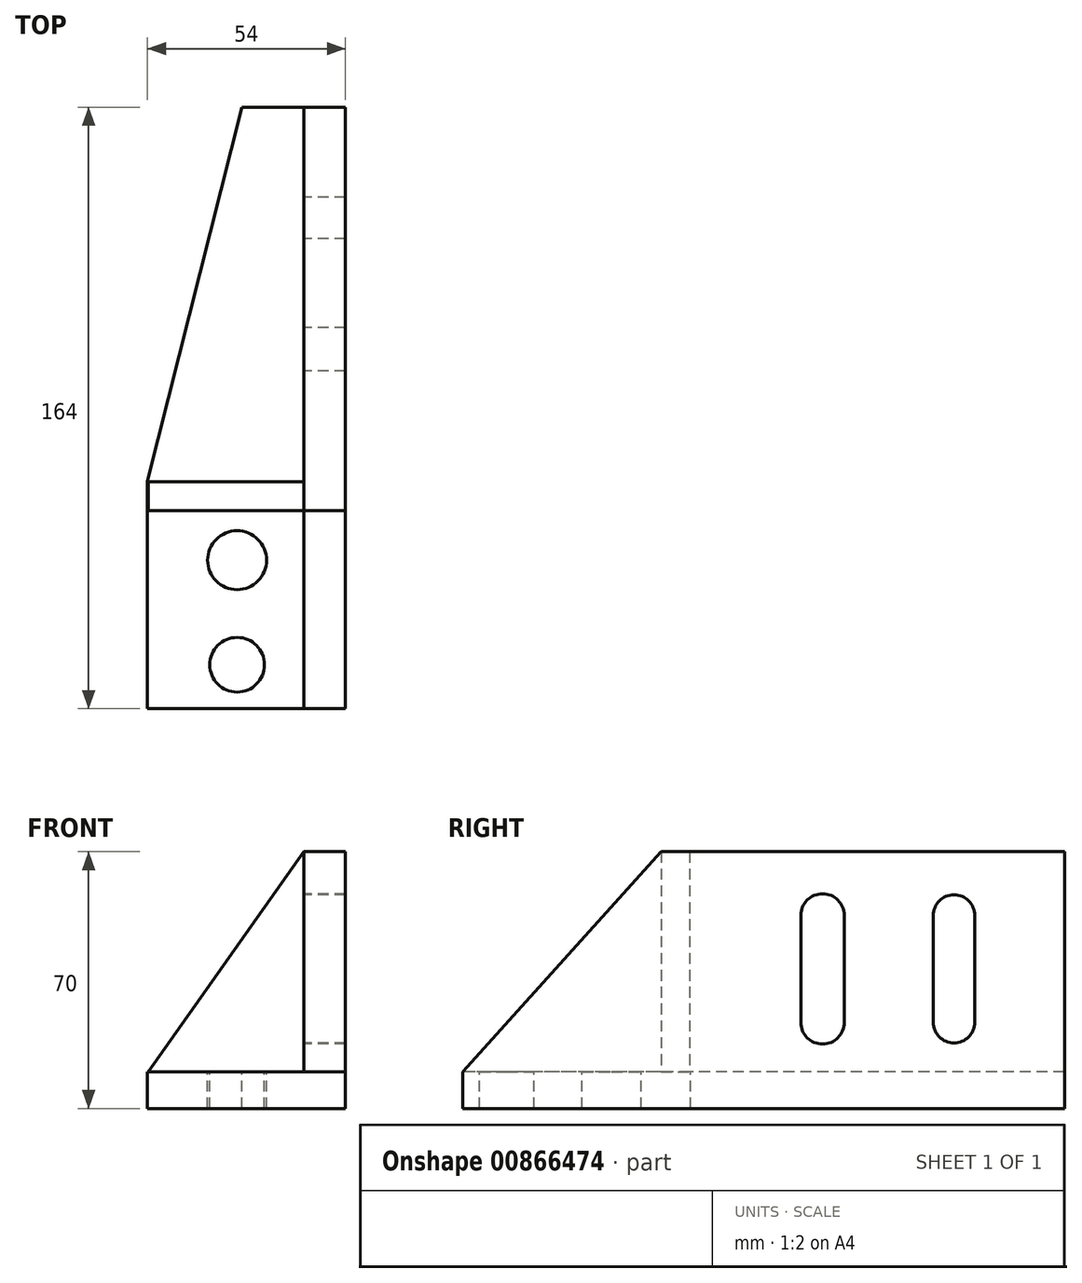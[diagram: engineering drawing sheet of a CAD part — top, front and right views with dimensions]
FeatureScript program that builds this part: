
annotation { "Feature Type Name" : "Feature", "Feature Type Description" : "" }
export const myFeature = defineFeature(function(context is Context, id is Id, definition is map)
    precondition{}
    {
        {
            var Q0;
            Q0=qCreatedBy(makeId("Top.planeOp"),FACE);
            var sketch = newSketch(context, id + "F0", { "sketchPlane" : qUnion([Q0])});
            skLineSegment(sketch, "E0.bottom", {"start": v(0, 0) * mm, "end": v(-54, 0) * mm});
            skLineSegment(sketch, "E0.top", {"start": v(0, -54) * mm, "end": v(-54, -54) * mm});
            skLineSegment(sketch, "E0.left", {"start": v(0, 0) * mm, "end": v(0, -54) * mm});
            skLineSegment(sketch, "E0.right", {"start": v(-54, 0) * mm, "end": v(-54, -54) * mm});
            skSolve(sketch);
        }
        {
            var Q0;
            Q0 = qSketchRegion(id + "F0", true);
            extrude(context, id + "F1", {"entities" : qUnion([Q0]), "depth" : 10 * mm, "offsetDistance" : 25 * mm});
        }
        {
            var Q0;
            Q0=makeQuery(id+"F1.opExtrude","SWEPT_FACE",FACE,{"disambiguationData":[OSD([sQuery(id+"F0.wireOp",EDGE,"E0.bottom")])]});
            extrude(context, id + "F2", {"entities" : qUnion([Q0]), "operationType" : NewBodyOperationType.ADD, "depth" : 110 * mm, "offsetDistance" : 25 * mm});
        }
        {
            var Q0;
            {var subQ0=sQuery(id+"F0.wireOp",EDGE,"E0.bottom");Q0=makeQuery(id+"F2.boolean.opBoolean","MERGE",FACE,{"derivedFrom":[makeQuery(id+"F1.opExtrude","CAP_FACE",FACE,{"disambiguationData":[OSD([subQ0,sQuery(id+"F0.wireOp",EDGE,"E0.top"),sQuery(id+"F0.wireOp",EDGE,"E0.left"),sQuery(id+"F0.wireOp",EDGE,"E0.right")])],"isStart":false}),makeQuery(id+"F2.opExtrude","SWEPT_FACE",FACE,{"disambiguationData":[OSD([subQ0]),TDD([makeQuery(id+"F1.opExtrude","CAP_EDGE",EDGE,{"disambiguationData":[OSD([subQ0])],"isStart":false})])]})]});}
            var sketch = newSketch(context, id + "F3", { "sketchPlane" : qUnion([Q0])});
            skLineSegment(sketch, "E1", {"start": v(-11.3, 110) * mm, "end": v(-11.3, -54) * mm});
            skSolve(sketch);
        }
        {
            var Q0;
            {var subQ0=sQuery(id+"F3.wireOp",EDGE,"E1");Q0=makeQuery(id+"F3.imprint","IMPRINT",FACE,{"disambiguationData":[TD([[makeQuery(id+"F3.imprint","IMPRINT",EDGE,{"derivedFrom":subQ0}),1.0]])]});}
            extrude(context, id + "F4", {"entities" : qUnion([Q0]), "operationType" : NewBodyOperationType.ADD, "depth" : 60 * mm, "offsetDistance" : 25 * mm});
        }
        {
            var Q0;
            Q0=makeQuery(id+"F4.opExtrude","SWEPT_FACE",FACE,{"disambiguationData":[OSD([sQuery(id+"F3.wireOp",EDGE,"E1")])]});
            var sketch = newSketch(context, id + "F5", { "sketchPlane" : qUnion([Q0])});
            skLineSegment(sketch, "E2", {"start": v(0, 70) * mm, "end": v(54, 10) * mm});
            skSolve(sketch);
        }
        {
            var Q0;
            Q0 = qSketchRegion(id + "F5", true);
            var Q1;
            {var subQ0=sQuery(id+"F5.wireOp",EDGE,"E2");Q1=makeQuery(id+"F5.imprint","IMPRINT",FACE,{"disambiguationData":[TD([[makeQuery(id+"F5.imprint","IMPRINT",EDGE,{"derivedFrom":subQ0}),1.0]])]});}
            extrude(context, id + "F6", {"entities" : qUnion([Q0, Q1]), "operationType" : NewBodyOperationType.REMOVE, "oppositeDirection" : true, "depth" : 25 * mm, "offsetDistance" : 25 * mm});
        }
        {
            var Q0;
            {var subQ0=sQuery(id+"F0.wireOp",EDGE,"E0.bottom");Q0=makeQuery(id+"F2.boolean.opBoolean","MERGE",FACE,{"derivedFrom":[makeQuery(id+"F1.opExtrude","CAP_FACE",FACE,{"disambiguationData":[OSD([subQ0,sQuery(id+"F0.wireOp",EDGE,"E0.top"),sQuery(id+"F0.wireOp",EDGE,"E0.left"),sQuery(id+"F0.wireOp",EDGE,"E0.right")])],"isStart":false}),makeQuery(id+"F2.opExtrude","SWEPT_FACE",FACE,{"disambiguationData":[OSD([subQ0]),TDD([makeQuery(id+"F1.opExtrude","CAP_EDGE",EDGE,{"disambiguationData":[OSD([subQ0])],"isStart":false})])]})]});}
            var sketch = newSketch(context, id + "F7", { "sketchPlane" : qUnion([Q0])});
            skSolve(sketch);
        }
        {
            var Q0;
            Q0=makeQuery(id+"F7.imprint","IMPRINT",FACE,{"disambiguationData":[TD([[makeQuery(id+"F7.imprint","IMPRINT",EDGE,{"derivedFrom":makeQuery(id+"F1.opExtrude","CAP_EDGE",EDGE,{"disambiguationData":[OSD([sQuery(id+"F0.wireOp",EDGE,"E0.top")])],"isStart":false})}),-1.0]])]});
            var sketch = newSketch(context, id + "F8", { "sketchPlane" : qUnion([Q0])});
            skLineSegment(sketch, "E3.bottom", {"start": v(-9.8, 0) * mm, "end": v(-53.8, 0) * mm});
            skLineSegment(sketch, "E3.top", {"start": v(-9.8, 7.85) * mm, "end": v(-53.8, 7.85) * mm});
            skLineSegment(sketch, "E3.left", {"start": v(-9.8, 0) * mm, "end": v(-9.8, 7.85) * mm});
            skLineSegment(sketch, "E3.right", {"start": v(-53.8, 0) * mm, "end": v(-53.8, 7.85) * mm});
            skSolve(sketch);
        }
        {
            var Q0;
            Q0 = qSketchRegion(id + "F8", true);
            extrude(context, id + "F9", {"entities" : qUnion([Q0]), "operationType" : NewBodyOperationType.ADD, "depth" : 60 * mm, "offsetDistance" : 25 * mm});
        }
        {
            var Q0;
            Q0=makeQuery(id+"F9.opExtrude","SWEPT_FACE",FACE,{"disambiguationData":[OSD([sQuery(id+"F8.wireOp",EDGE,"E3.bottom")])]});
            var sketch = newSketch(context, id + "F10", { "sketchPlane" : qUnion([Q0])});
            skLineSegment(sketch, "E4", {"start": v(-11.3, 70) * mm, "end": v(-53.8, 10) * mm});
            skSolve(sketch);
        }
        {
            var Q0;
            Q0 = qSketchRegion(id + "F10", true);
            var Q1;
            Q1=makeQuery(id+"F10.imprint","IMPRINT",FACE,{"disambiguationData":[TD([[makeQuery(id+"F10.imprint","IMPRINT",EDGE,{"derivedFrom":sQuery(id+"F10.wireOp",EDGE,"E4")}),-1.0]])]});
            extrude(context, id + "F11", {"entities" : qUnion([Q0, Q1]), "operationType" : NewBodyOperationType.REMOVE, "oppositeDirection" : true, "depth" : 25 * mm, "offsetDistance" : 25 * mm});
        }
        {
            var Q0;
            Q0=makeQuery(id+"F7.imprint","IMPRINT",FACE,{"disambiguationData":[TD([[makeQuery(id+"F7.imprint","IMPRINT",EDGE,{"derivedFrom":makeQuery(id+"F1.opExtrude","CAP_EDGE",EDGE,{"disambiguationData":[OSD([sQuery(id+"F0.wireOp",EDGE,"E0.top")])],"isStart":false})}),-1.0]])]});
            var sketch = newSketch(context, id + "F12", { "sketchPlane" : qUnion([Q0])});
            skCircle(sketch, "E5", {"center": v(-29.54, -13.5) * mm, "radius": 8.03 * mm});
            skCircle(sketch, "E6", {"center": v(-29.54, -42.01) * mm, "radius": 7.46 * mm});
            skSolve(sketch);
        }
        {
            var Q0;
            Q0 = qSketchRegion(id + "F12", true);
            extrude(context, id + "F13", {"entities" : qUnion([Q0]), "operationType" : NewBodyOperationType.REMOVE, "oppositeDirection" : true, "depth" : 25 * mm, "offsetDistance" : 25 * mm});
        }
        {
            var Q0;
            {var subQ0=sQuery(id+"F0.wireOp",EDGE,"E0.bottom");var subQ1=sQuery(id+"F3.wireOp",EDGE,"E1");Q0=makeQuery(id+"F9.boolean.opBoolean","SPLIT",FACE,{"disambiguationData":[TD([makeQuery(id+"F2.opExtrude","CAP_FACE",FACE,{"disambiguationData":[OSD([subQ0])],"isStart":false})])],"derivedFrom":makeQuery(id+"F4.opExtrude","SWEPT_FACE",FACE,{"disambiguationData":[OSD([subQ1])]})});}
            var sketch = newSketch(context, id + "F14", { "sketchPlane" : qUnion([Q0])});
            skLineSegment(sketch, "E7.bottom", {"start": v(-85.53, 52.63) * mm, "end": v(-74.25, 52.63) * mm});
            skLineSegment(sketch, "E7.top", {"start": v(-85.53, 23.5) * mm, "end": v(-74.25, 23.5) * mm});
            skLineSegment(sketch, "E7.left", {"start": v(-85.53, 52.63) * mm, "end": v(-85.53, 23.5) * mm});
            skLineSegment(sketch, "E7.right", {"start": v(-74.25, 52.63) * mm, "end": v(-74.25, 23.5) * mm});
            skLineSegment(sketch, "E8.bottom", {"start": v(-49.99, 52.63) * mm, "end": v(-38.14, 52.63) * mm});
            skLineSegment(sketch, "E8.top", {"start": v(-49.99, 23.5) * mm, "end": v(-38.14, 23.5) * mm});
            skLineSegment(sketch, "E8.left", {"start": v(-49.99, 52.63) * mm, "end": v(-49.99, 23.5) * mm});
            skLineSegment(sketch, "E8.right", {"start": v(-38.14, 52.63) * mm, "end": v(-38.14, 23.5) * mm});
            skArc(sketch, "E9", {"start": v(-74.25, 52.63) * mm, "mid": v(-79.89, 58.27) * mm, "end": v(-85.53, 52.63) * mm});
            skArc(sketch, "E10", {"start": v(-85.53, 23.5) * mm, "mid": v(-79.89, 17.86) * mm, "end": v(-74.25, 23.5) * mm});
            skArc(sketch, "E11", {"start": v(-38.14, 52.63) * mm, "mid": v(-44.06, 58.55) * mm, "end": v(-49.99, 52.63) * mm});
            skArc(sketch, "E12", {"start": v(-49.99, 23.5) * mm, "mid": v(-44.06, 17.58) * mm, "end": v(-38.14, 23.5) * mm});
            skSolve(sketch);
        }
        {
            var Q0;
            Q0 = qSketchRegion(id + "F14", true);
            extrude(context, id + "F15", {"entities" : qUnion([Q0]), "operationType" : NewBodyOperationType.REMOVE, "oppositeDirection" : true, "depth" : 25 * mm, "offsetDistance" : 25 * mm});
        }
        {
            var Q0;
            Q0=makeQuery(id+"F7.imprint","IMPRINT",FACE,{"disambiguationData":[TD([[makeQuery(id+"F7.imprint","IMPRINT",EDGE,{"derivedFrom":makeQuery(id+"F1.opExtrude","CAP_EDGE",EDGE,{"disambiguationData":[OSD([sQuery(id+"F0.wireOp",EDGE,"E0.top")])],"isStart":false})}),-1.0]])]});
            var sketch = newSketch(context, id + "F16", { "sketchPlane" : qUnion([Q0])});
            skLineSegment(sketch, "E13", {"start": v(-10.93, 110.11) * mm, "end": v(-28.2, 110.11) * mm});
            skLineSegment(sketch, "E14", {"start": v(-28.2, 110.11) * mm, "end": v(-54.05, 7.83) * mm});
            skSolve(sketch);
        }
        {
            var Q0;
            Q0 = qSketchRegion(id + "F16", true);
            var Q1;
            {var subQ0=sQuery(id+"F16.wireOp",EDGE,"E14");var subQ2=sQuery(id+"F0.wireOp",EDGE,"E0.bottom");var subQ5=makeQuery(id+"F7.imprint","IMPRINT",EDGE,{"derivedFrom":makeQuery(id+"F2.opExtrude","CAP_EDGE",EDGE,{"disambiguationData":[OSD([subQ2]),TDD([makeQuery(id+"F1.opExtrude","CAP_EDGE",EDGE,{"disambiguationData":[OSD([subQ2])],"isStart":false})])],"isStart":false})});var subQ6=makeQuery(id+"F16.imprint","INTERSECT",VERTEX,{"derivedFrom":[subQ5,subQ0]});Q1=makeQuery(id+"F16.imprint","IMPRINT",FACE,{"disambiguationData":[TD([[makeQuery(id+"F16.imprint","IMPRINT",EDGE,{"disambiguationData":[TD([[subQ6,-1.0]])],"derivedFrom":subQ0}),-1.0]])]});}
            extrude(context, id + "F17", {"entities" : qUnion([Q0, Q1]), "operationType" : NewBodyOperationType.REMOVE, "oppositeDirection" : true, "depth" : 25 * mm, "offsetDistance" : 25 * mm});
        }
    });
